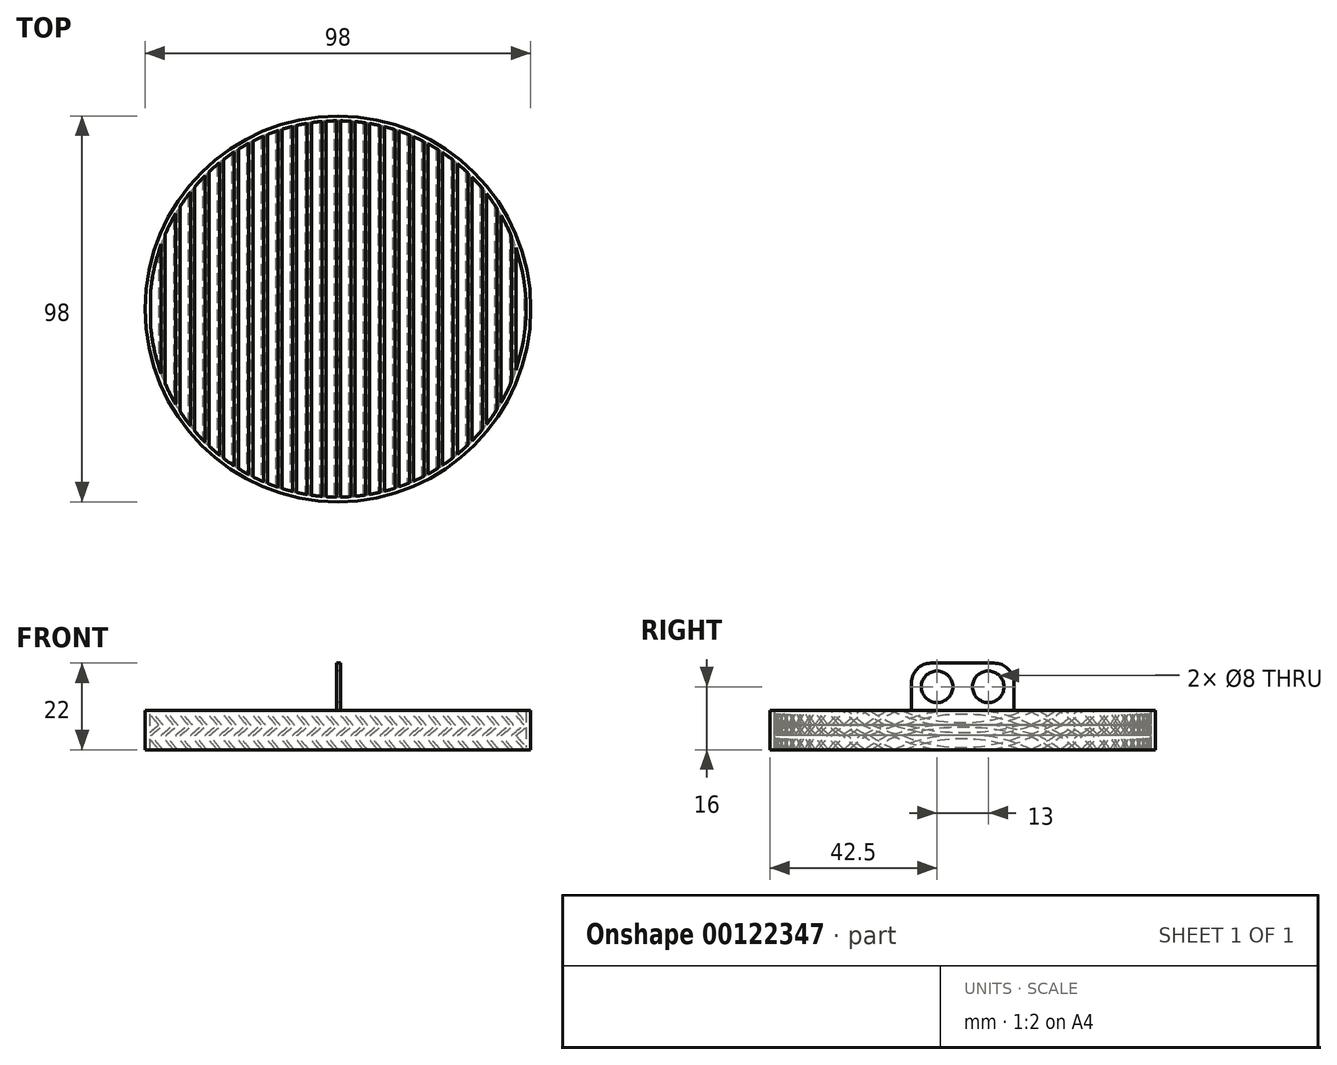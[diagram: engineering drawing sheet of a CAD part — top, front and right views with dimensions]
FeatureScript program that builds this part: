
annotation { "Feature Type Name" : "Feature", "Feature Type Description" : "" }
export const myFeature = defineFeature(function(context is Context, id is Id, definition is map)
    precondition{}
    {
        {
            var Q0;
            Q0=qCreatedBy(makeId("Top.planeOp"),FACE);
            var sketch = newSketch(context, id + "F0", { "sketchPlane" : qUnion([Q0])});
            skCircle(sketch, "E0", {"center": v(0, 0) * mm, "radius": 49 * mm});
            skCircle(sketch, "E1", {"center": v(0, 0) * mm, "radius": 47.8 * mm});
            skSolve(sketch);
        }
        {
            var Q0;
            Q0=makeQuery(id+"F0.imprint","IMPRINT",FACE,{"disambiguationData":[TD([[makeQuery(id+"F0.imprint","IMPRINT",EDGE,{"derivedFrom":sQuery(id+"F0.wireOp",EDGE,"E0")}),1.0]])]});
            extrude(context, id + "F1", {"entities" : qUnion([Q0]), "depth" : 10 * mm});
        }
        {
            var Q0;
            Q0=qCreatedBy(makeId("Front.planeOp"),FACE);
            var sketch = newSketch(context, id + "F2", { "sketchPlane" : qUnion([Q0])});
            skLineSegment(sketch, "E2", {"start": v(-45.5, 0) * mm, "end": v(-48.6, 3.7) * mm});
            skLineSegment(sketch, "E3", {"start": v(-48.6, 3.7) * mm, "end": v(-45.5, 6.3) * mm});
            skLineSegment(sketch, "E4", {"start": v(-45.5, 6.3) * mm, "end": v(-48.6, 10) * mm});
            skLineSegment(sketch, "E5.0", {"start": v(-44.37, 6.2) * mm, "end": v(-47.56, 10) * mm});
            skLineSegment(sketch, "E5.1", {"start": v(-47.47, 3.6) * mm, "end": v(-44.37, 6.2) * mm});
            skLineSegment(sketch, "E5.2", {"start": v(-44.45, 0) * mm, "end": v(-47.47, 3.6) * mm});
            skLineSegment(sketch, "E6", {"start": v(-48.6, 10) * mm, "end": v(-47.56, 10) * mm});
            skLineSegment(sketch, "E7", {"start": v(-45.5, 0) * mm, "end": v(-44.45, 0) * mm});
            skLineSegment(sketch, "E8.1.0.0", {"start": v(-40.74, 0) * mm, "end": v(-43.76, 3.6) * mm});
            skLineSegment(sketch, "E8.1.0.1", {"start": v(-43.76, 3.6) * mm, "end": v(-40.66, 6.2) * mm});
            skLineSegment(sketch, "E8.1.0.2", {"start": v(-44.9, 3.7) * mm, "end": v(-41.79, 6.3) * mm});
            skLineSegment(sketch, "E8.1.0.3", {"start": v(-40.66, 6.2) * mm, "end": v(-43.85, 10) * mm});
            skLineSegment(sketch, "E8.1.0.4", {"start": v(-41.79, 6.3) * mm, "end": v(-44.9, 10) * mm});
            skLineSegment(sketch, "E8.1.0.5", {"start": v(-41.79, 0) * mm, "end": v(-44.9, 3.7) * mm});
            skLineSegment(sketch, "E8.1.0.6", {"start": v(-44.9, 10) * mm, "end": v(-43.85, 10) * mm});
            skLineSegment(sketch, "E8.1.0.7", {"start": v(-41.79, 0) * mm, "end": v(-40.74, 0) * mm});
            skLineSegment(sketch, "E8.2.0.0", {"start": v(-37.03, 0) * mm, "end": v(-40.05, 3.6) * mm});
            skLineSegment(sketch, "E8.2.0.1", {"start": v(-40.05, 3.6) * mm, "end": v(-36.95, 6.2) * mm});
            skLineSegment(sketch, "E8.2.0.2", {"start": v(-41.18, 3.7) * mm, "end": v(-38.08, 6.3) * mm});
            skLineSegment(sketch, "E8.2.0.3", {"start": v(-36.95, 6.2) * mm, "end": v(-40.14, 10) * mm});
            skLineSegment(sketch, "E8.2.0.4", {"start": v(-38.08, 6.3) * mm, "end": v(-41.18, 10) * mm});
            skLineSegment(sketch, "E8.2.0.5", {"start": v(-38.08, 0) * mm, "end": v(-41.18, 3.7) * mm});
            skLineSegment(sketch, "E8.2.0.6", {"start": v(-41.18, 10) * mm, "end": v(-40.14, 10) * mm});
            skLineSegment(sketch, "E8.2.0.7", {"start": v(-38.08, 0) * mm, "end": v(-37.03, 0) * mm});
            skLineSegment(sketch, "E8.3.0.0", {"start": v(-33.32, 0) * mm, "end": v(-36.34, 3.6) * mm});
            skLineSegment(sketch, "E8.3.0.1", {"start": v(-36.34, 3.6) * mm, "end": v(-33.24, 6.2) * mm});
            skLineSegment(sketch, "E8.3.0.2", {"start": v(-37.47, 3.7) * mm, "end": v(-34.37, 6.3) * mm});
            skLineSegment(sketch, "E8.3.0.3", {"start": v(-33.24, 6.2) * mm, "end": v(-36.43, 10) * mm});
            skLineSegment(sketch, "E8.3.0.4", {"start": v(-34.37, 6.3) * mm, "end": v(-37.47, 10) * mm});
            skLineSegment(sketch, "E8.3.0.5", {"start": v(-34.37, 0) * mm, "end": v(-37.47, 3.7) * mm});
            skLineSegment(sketch, "E8.3.0.6", {"start": v(-37.47, 10) * mm, "end": v(-36.43, 10) * mm});
            skLineSegment(sketch, "E8.3.0.7", {"start": v(-34.37, 0) * mm, "end": v(-33.32, 0) * mm});
            skLineSegment(sketch, "E8.4.0.0", {"start": v(-29.61, 0) * mm, "end": v(-32.63, 3.6) * mm});
            skLineSegment(sketch, "E8.4.0.1", {"start": v(-32.63, 3.6) * mm, "end": v(-29.53, 6.2) * mm});
            skLineSegment(sketch, "E8.4.0.2", {"start": v(-33.76, 3.7) * mm, "end": v(-30.66, 6.3) * mm});
            skLineSegment(sketch, "E8.4.0.3", {"start": v(-29.53, 6.2) * mm, "end": v(-32.72, 10) * mm});
            skLineSegment(sketch, "E8.4.0.4", {"start": v(-30.66, 6.3) * mm, "end": v(-33.76, 10) * mm});
            skLineSegment(sketch, "E8.4.0.5", {"start": v(-30.66, 0) * mm, "end": v(-33.76, 3.7) * mm});
            skLineSegment(sketch, "E8.4.0.6", {"start": v(-33.76, 10) * mm, "end": v(-32.72, 10) * mm});
            skLineSegment(sketch, "E8.4.0.7", {"start": v(-30.66, 0) * mm, "end": v(-29.61, 0) * mm});
            skLineSegment(sketch, "E8.5.0.0", {"start": v(-25.9, 0) * mm, "end": v(-28.92, 3.6) * mm});
            skLineSegment(sketch, "E8.5.0.1", {"start": v(-28.92, 3.6) * mm, "end": v(-25.82, 6.2) * mm});
            skLineSegment(sketch, "E8.5.0.2", {"start": v(-30.05, 3.7) * mm, "end": v(-26.95, 6.3) * mm});
            skLineSegment(sketch, "E8.5.0.3", {"start": v(-25.82, 6.2) * mm, "end": v(-29, 10) * mm});
            skLineSegment(sketch, "E8.5.0.4", {"start": v(-26.95, 6.3) * mm, "end": v(-30.05, 10) * mm});
            skLineSegment(sketch, "E8.5.0.5", {"start": v(-26.95, 0) * mm, "end": v(-30.05, 3.7) * mm});
            skLineSegment(sketch, "E8.5.0.6", {"start": v(-30.05, 10) * mm, "end": v(-29, 10) * mm});
            skLineSegment(sketch, "E8.5.0.7", {"start": v(-26.95, 0) * mm, "end": v(-25.9, 0) * mm});
            skLineSegment(sketch, "E8.6.0.0", {"start": v(-22.2, 0) * mm, "end": v(-25.21, 3.6) * mm});
            skLineSegment(sketch, "E8.6.0.1", {"start": v(-25.21, 3.6) * mm, "end": v(-22.1, 6.2) * mm});
            skLineSegment(sketch, "E8.6.0.2", {"start": v(-26.34, 3.7) * mm, "end": v(-23.24, 6.3) * mm});
            skLineSegment(sketch, "E8.6.0.3", {"start": v(-22.1, 6.2) * mm, "end": v(-25.3, 10) * mm});
            skLineSegment(sketch, "E8.6.0.4", {"start": v(-23.24, 6.3) * mm, "end": v(-26.34, 10) * mm});
            skLineSegment(sketch, "E8.6.0.5", {"start": v(-23.24, 0) * mm, "end": v(-26.34, 3.7) * mm});
            skLineSegment(sketch, "E8.6.0.6", {"start": v(-26.34, 10) * mm, "end": v(-25.3, 10) * mm});
            skLineSegment(sketch, "E8.6.0.7", {"start": v(-23.24, 0) * mm, "end": v(-22.2, 0) * mm});
            skLineSegment(sketch, "E8.7.0.0", {"start": v(-18.48, 0) * mm, "end": v(-21.5, 3.6) * mm});
            skLineSegment(sketch, "E8.7.0.1", {"start": v(-21.5, 3.6) * mm, "end": v(-18.4, 6.2) * mm});
            skLineSegment(sketch, "E8.7.0.2", {"start": v(-22.63, 3.7) * mm, "end": v(-19.53, 6.3) * mm});
            skLineSegment(sketch, "E8.7.0.3", {"start": v(-18.4, 6.2) * mm, "end": v(-21.59, 10) * mm});
            skLineSegment(sketch, "E8.7.0.4", {"start": v(-19.53, 6.3) * mm, "end": v(-22.63, 10) * mm});
            skLineSegment(sketch, "E8.7.0.5", {"start": v(-19.53, 0) * mm, "end": v(-22.63, 3.7) * mm});
            skLineSegment(sketch, "E8.7.0.6", {"start": v(-22.63, 10) * mm, "end": v(-21.59, 10) * mm});
            skLineSegment(sketch, "E8.7.0.7", {"start": v(-19.53, 0) * mm, "end": v(-18.48, 0) * mm});
            skLineSegment(sketch, "E8.8.0.0", {"start": v(-14.77, 0) * mm, "end": v(-17.8, 3.6) * mm});
            skLineSegment(sketch, "E8.8.0.1", {"start": v(-17.8, 3.6) * mm, "end": v(-14.69, 6.2) * mm});
            skLineSegment(sketch, "E8.8.0.2", {"start": v(-18.92, 3.7) * mm, "end": v(-15.82, 6.3) * mm});
            skLineSegment(sketch, "E8.8.0.3", {"start": v(-14.69, 6.2) * mm, "end": v(-17.88, 10) * mm});
            skLineSegment(sketch, "E8.8.0.4", {"start": v(-15.82, 6.3) * mm, "end": v(-18.92, 10) * mm});
            skLineSegment(sketch, "E8.8.0.5", {"start": v(-15.82, 0) * mm, "end": v(-18.92, 3.7) * mm});
            skLineSegment(sketch, "E8.8.0.6", {"start": v(-18.92, 10) * mm, "end": v(-17.88, 10) * mm});
            skLineSegment(sketch, "E8.8.0.7", {"start": v(-15.82, 0) * mm, "end": v(-14.77, 0) * mm});
            skLineSegment(sketch, "E8.9.0.0", {"start": v(-11.06, 0) * mm, "end": v(-14.08, 3.6) * mm});
            skLineSegment(sketch, "E8.9.0.1", {"start": v(-14.08, 3.6) * mm, "end": v(-10.98, 6.2) * mm});
            skLineSegment(sketch, "E8.9.0.2", {"start": v(-15.2, 3.7) * mm, "end": v(-12.1, 6.3) * mm});
            skLineSegment(sketch, "E8.9.0.3", {"start": v(-10.98, 6.2) * mm, "end": v(-14.17, 10) * mm});
            skLineSegment(sketch, "E8.9.0.4", {"start": v(-12.1, 6.3) * mm, "end": v(-15.2, 10) * mm});
            skLineSegment(sketch, "E8.9.0.5", {"start": v(-12.1, 0) * mm, "end": v(-15.21, 3.7) * mm});
            skLineSegment(sketch, "E8.9.0.6", {"start": v(-15.2, 10) * mm, "end": v(-14.17, 10) * mm});
            skLineSegment(sketch, "E8.9.0.7", {"start": v(-12.1, 0) * mm, "end": v(-11.06, 0) * mm});
            skLineSegment(sketch, "E8.10.0.0", {"start": v(-7.35, 0) * mm, "end": v(-10.37, 3.6) * mm});
            skLineSegment(sketch, "E8.10.0.1", {"start": v(-10.37, 3.6) * mm, "end": v(-7.27, 6.2) * mm});
            skLineSegment(sketch, "E8.10.0.2", {"start": v(-11.5, 3.7) * mm, "end": v(-8.4, 6.3) * mm});
            skLineSegment(sketch, "E8.10.0.3", {"start": v(-7.27, 6.2) * mm, "end": v(-10.46, 10) * mm});
            skLineSegment(sketch, "E8.10.0.4", {"start": v(-8.4, 6.3) * mm, "end": v(-11.5, 10) * mm});
            skLineSegment(sketch, "E8.10.0.5", {"start": v(-8.4, 0) * mm, "end": v(-11.5, 3.7) * mm});
            skLineSegment(sketch, "E8.10.0.6", {"start": v(-11.5, 10) * mm, "end": v(-10.46, 10) * mm});
            skLineSegment(sketch, "E8.10.0.7", {"start": v(-8.4, 0) * mm, "end": v(-7.35, 0) * mm});
            skLineSegment(sketch, "E8.11.0.0", {"start": v(-3.64, 0) * mm, "end": v(-6.66, 3.6) * mm});
            skLineSegment(sketch, "E8.11.0.1", {"start": v(-6.66, 3.6) * mm, "end": v(-3.56, 6.2) * mm});
            skLineSegment(sketch, "E8.11.0.2", {"start": v(-7.79, 3.7) * mm, "end": v(-4.69, 6.3) * mm});
            skLineSegment(sketch, "E8.11.0.3", {"start": v(-3.56, 6.2) * mm, "end": v(-6.75, 10) * mm});
            skLineSegment(sketch, "E8.11.0.4", {"start": v(-4.69, 6.3) * mm, "end": v(-7.8, 10) * mm});
            skLineSegment(sketch, "E8.11.0.5", {"start": v(-4.69, 0) * mm, "end": v(-7.8, 3.7) * mm});
            skLineSegment(sketch, "E8.11.0.6", {"start": v(-7.79, 10) * mm, "end": v(-6.75, 10) * mm});
            skLineSegment(sketch, "E8.11.0.7", {"start": v(-4.69, 0) * mm, "end": v(-3.64, 0) * mm});
            skLineSegment(sketch, "E8.12.0.0", {"start": v(0.07, 0) * mm, "end": v(-2.95, 3.6) * mm});
            skLineSegment(sketch, "E8.12.0.1", {"start": v(-2.95, 3.6) * mm, "end": v(0.15, 6.2) * mm});
            skLineSegment(sketch, "E8.12.0.2", {"start": v(-4.08, 3.7) * mm, "end": v(-0.98, 6.3) * mm});
            skLineSegment(sketch, "E8.12.0.3", {"start": v(0.15, 6.2) * mm, "end": v(-3.04, 10) * mm});
            skLineSegment(sketch, "E8.12.0.4", {"start": v(-0.98, 6.3) * mm, "end": v(-4.08, 10) * mm});
            skLineSegment(sketch, "E8.12.0.5", {"start": v(-0.98, 0) * mm, "end": v(-4.08, 3.7) * mm});
            skLineSegment(sketch, "E8.12.0.6", {"start": v(-4.08, 10) * mm, "end": v(-3.04, 10) * mm});
            skLineSegment(sketch, "E8.12.0.7", {"start": v(-0.98, 0) * mm, "end": v(0.07, 0) * mm});
            skLineSegment(sketch, "E8.13.0.0", {"start": v(3.78, 0) * mm, "end": v(0.76, 3.6) * mm});
            skLineSegment(sketch, "E8.13.0.1", {"start": v(0.76, 3.6) * mm, "end": v(3.86, 6.2) * mm});
            skLineSegment(sketch, "E8.13.0.2", {"start": v(-0.37, 3.7) * mm, "end": v(2.73, 6.3) * mm});
            skLineSegment(sketch, "E8.13.0.3", {"start": v(3.86, 6.2) * mm, "end": v(0.67, 10) * mm});
            skLineSegment(sketch, "E8.13.0.4", {"start": v(2.73, 6.3) * mm, "end": v(-0.37, 10) * mm});
            skLineSegment(sketch, "E8.13.0.5", {"start": v(2.73, 0) * mm, "end": v(-0.37, 3.7) * mm});
            skLineSegment(sketch, "E8.13.0.6", {"start": v(-0.37, 10) * mm, "end": v(0.67, 10) * mm});
            skLineSegment(sketch, "E8.13.0.7", {"start": v(2.73, 0) * mm, "end": v(3.78, 0) * mm});
            skLineSegment(sketch, "E8.14.0.0", {"start": v(7.49, 0) * mm, "end": v(4.47, 3.6) * mm});
            skLineSegment(sketch, "E8.14.0.1", {"start": v(4.47, 3.6) * mm, "end": v(7.57, 6.2) * mm});
            skLineSegment(sketch, "E8.14.0.2", {"start": v(3.34, 3.7) * mm, "end": v(6.44, 6.3) * mm});
            skLineSegment(sketch, "E8.14.0.3", {"start": v(7.57, 6.2) * mm, "end": v(4.38, 10) * mm});
            skLineSegment(sketch, "E8.14.0.4", {"start": v(6.44, 6.3) * mm, "end": v(3.34, 10) * mm});
            skLineSegment(sketch, "E8.14.0.5", {"start": v(6.44, 0) * mm, "end": v(3.34, 3.7) * mm});
            skLineSegment(sketch, "E8.14.0.6", {"start": v(3.34, 10) * mm, "end": v(4.38, 10) * mm});
            skLineSegment(sketch, "E8.14.0.7", {"start": v(6.44, 0) * mm, "end": v(7.49, 0) * mm});
            skLineSegment(sketch, "E8.direction1", {"start": v(-45.5, 0) * mm, "end": v(-41.79, 0) * mm, "construction": true});
            skLineSegment(sketch, "E9.0.15.0", {"start": v(11.2, 0) * mm, "end": v(8.18, 3.6) * mm});
            skLineSegment(sketch, "E9.3.15.0", {"start": v(8.18, 3.6) * mm, "end": v(11.28, 6.2) * mm});
            skLineSegment(sketch, "E9.6.15.0", {"start": v(7.05, 3.7) * mm, "end": v(10.15, 6.3) * mm});
            skLineSegment(sketch, "E9.9.15.0", {"start": v(11.28, 6.2) * mm, "end": v(8.1, 10) * mm});
            skLineSegment(sketch, "E9.12.15.0", {"start": v(10.15, 6.3) * mm, "end": v(7.05, 10) * mm});
            skLineSegment(sketch, "E9.15.15.0", {"start": v(10.15, 0) * mm, "end": v(7.05, 3.7) * mm});
            skLineSegment(sketch, "E9.18.15.0", {"start": v(7.05, 10) * mm, "end": v(8.1, 10) * mm});
            skLineSegment(sketch, "E9.21.15.0", {"start": v(10.15, 0) * mm, "end": v(11.2, 0) * mm});
            skLineSegment(sketch, "E9.0.16.0", {"start": v(14.9, 0) * mm, "end": v(11.89, 3.6) * mm});
            skLineSegment(sketch, "E9.3.16.0", {"start": v(11.89, 3.6) * mm, "end": v(15, 6.2) * mm});
            skLineSegment(sketch, "E9.6.16.0", {"start": v(10.76, 3.7) * mm, "end": v(13.86, 6.3) * mm});
            skLineSegment(sketch, "E9.9.16.0", {"start": v(15, 6.2) * mm, "end": v(11.8, 10) * mm});
            skLineSegment(sketch, "E9.12.16.0", {"start": v(13.86, 6.3) * mm, "end": v(10.76, 10) * mm});
            skLineSegment(sketch, "E9.15.16.0", {"start": v(13.86, 0) * mm, "end": v(10.76, 3.7) * mm});
            skLineSegment(sketch, "E9.18.16.0", {"start": v(10.76, 10) * mm, "end": v(11.8, 10) * mm});
            skLineSegment(sketch, "E9.21.16.0", {"start": v(13.86, 0) * mm, "end": v(14.9, 0) * mm});
            skLineSegment(sketch, "E9.0.17.0", {"start": v(18.62, 0) * mm, "end": v(15.6, 3.6) * mm});
            skLineSegment(sketch, "E9.3.17.0", {"start": v(15.6, 3.6) * mm, "end": v(18.7, 6.2) * mm});
            skLineSegment(sketch, "E9.6.17.0", {"start": v(14.47, 3.7) * mm, "end": v(17.57, 6.3) * mm});
            skLineSegment(sketch, "E9.9.17.0", {"start": v(18.7, 6.2) * mm, "end": v(15.51, 10) * mm});
            skLineSegment(sketch, "E9.12.17.0", {"start": v(17.57, 6.3) * mm, "end": v(14.47, 10) * mm});
            skLineSegment(sketch, "E9.15.17.0", {"start": v(17.57, 0) * mm, "end": v(14.47, 3.7) * mm});
            skLineSegment(sketch, "E9.18.17.0", {"start": v(14.47, 10) * mm, "end": v(15.51, 10) * mm});
            skLineSegment(sketch, "E9.21.17.0", {"start": v(17.57, 0) * mm, "end": v(18.62, 0) * mm});
            skLineSegment(sketch, "E9.0.18.0", {"start": v(22.33, 0) * mm, "end": v(19.3, 3.6) * mm});
            skLineSegment(sketch, "E9.3.18.0", {"start": v(19.3, 3.6) * mm, "end": v(22.41, 6.2) * mm});
            skLineSegment(sketch, "E9.6.18.0", {"start": v(18.18, 3.7) * mm, "end": v(21.28, 6.3) * mm});
            skLineSegment(sketch, "E9.9.18.0", {"start": v(22.41, 6.2) * mm, "end": v(19.22, 10) * mm});
            skLineSegment(sketch, "E9.12.18.0", {"start": v(21.28, 6.3) * mm, "end": v(18.18, 10) * mm});
            skLineSegment(sketch, "E9.15.18.0", {"start": v(21.28, 0) * mm, "end": v(18.18, 3.7) * mm});
            skLineSegment(sketch, "E9.18.18.0", {"start": v(18.18, 10) * mm, "end": v(19.22, 10) * mm});
            skLineSegment(sketch, "E9.21.18.0", {"start": v(21.28, 0) * mm, "end": v(22.33, 0) * mm});
            skLineSegment(sketch, "E9.0.19.0", {"start": v(26.04, 0) * mm, "end": v(23.02, 3.6) * mm});
            skLineSegment(sketch, "E9.3.19.0", {"start": v(23.02, 3.6) * mm, "end": v(26.12, 6.2) * mm});
            skLineSegment(sketch, "E9.6.19.0", {"start": v(21.89, 3.7) * mm, "end": v(25, 6.3) * mm});
            skLineSegment(sketch, "E9.9.19.0", {"start": v(26.12, 6.2) * mm, "end": v(22.93, 10) * mm});
            skLineSegment(sketch, "E9.12.19.0", {"start": v(25, 6.3) * mm, "end": v(21.9, 10) * mm});
            skLineSegment(sketch, "E9.15.19.0", {"start": v(25, 0) * mm, "end": v(21.89, 3.7) * mm});
            skLineSegment(sketch, "E9.18.19.0", {"start": v(21.9, 10) * mm, "end": v(22.93, 10) * mm});
            skLineSegment(sketch, "E9.21.19.0", {"start": v(25, 0) * mm, "end": v(26.04, 0) * mm});
            skLineSegment(sketch, "E10.0.20.0", {"start": v(29.75, 0) * mm, "end": v(26.73, 3.6) * mm});
            skLineSegment(sketch, "E10.3.20.0", {"start": v(26.73, 3.6) * mm, "end": v(29.83, 6.2) * mm});
            skLineSegment(sketch, "E10.6.20.0", {"start": v(25.6, 3.7) * mm, "end": v(28.7, 6.3) * mm});
            skLineSegment(sketch, "E10.9.20.0", {"start": v(29.83, 6.2) * mm, "end": v(26.64, 10) * mm});
            skLineSegment(sketch, "E10.12.20.0", {"start": v(28.7, 6.3) * mm, "end": v(25.6, 10) * mm});
            skLineSegment(sketch, "E10.15.20.0", {"start": v(28.7, 0) * mm, "end": v(25.6, 3.7) * mm});
            skLineSegment(sketch, "E10.18.20.0", {"start": v(25.6, 10) * mm, "end": v(26.64, 10) * mm});
            skLineSegment(sketch, "E10.21.20.0", {"start": v(28.7, 0) * mm, "end": v(29.75, 0) * mm});
            skLineSegment(sketch, "E10.0.21.0", {"start": v(33.46, 0) * mm, "end": v(30.44, 3.6) * mm});
            skLineSegment(sketch, "E10.3.21.0", {"start": v(30.44, 3.6) * mm, "end": v(33.54, 6.2) * mm});
            skLineSegment(sketch, "E10.6.21.0", {"start": v(29.3, 3.7) * mm, "end": v(32.41, 6.3) * mm});
            skLineSegment(sketch, "E10.9.21.0", {"start": v(33.54, 6.2) * mm, "end": v(30.35, 10) * mm});
            skLineSegment(sketch, "E10.12.21.0", {"start": v(32.41, 6.3) * mm, "end": v(29.31, 10) * mm});
            skLineSegment(sketch, "E10.15.21.0", {"start": v(32.41, 0) * mm, "end": v(29.3, 3.7) * mm});
            skLineSegment(sketch, "E10.18.21.0", {"start": v(29.31, 10) * mm, "end": v(30.35, 10) * mm});
            skLineSegment(sketch, "E10.21.21.0", {"start": v(32.41, 0) * mm, "end": v(33.46, 0) * mm});
            skLineSegment(sketch, "E10.0.22.0", {"start": v(37.17, 0) * mm, "end": v(34.15, 3.6) * mm});
            skLineSegment(sketch, "E10.3.22.0", {"start": v(34.15, 3.6) * mm, "end": v(37.25, 6.2) * mm});
            skLineSegment(sketch, "E10.6.22.0", {"start": v(33.02, 3.7) * mm, "end": v(36.12, 6.3) * mm});
            skLineSegment(sketch, "E10.9.22.0", {"start": v(37.25, 6.2) * mm, "end": v(34.06, 10) * mm});
            skLineSegment(sketch, "E10.12.22.0", {"start": v(36.12, 6.3) * mm, "end": v(33.02, 10) * mm});
            skLineSegment(sketch, "E10.15.22.0", {"start": v(36.12, 0) * mm, "end": v(33.02, 3.7) * mm});
            skLineSegment(sketch, "E10.18.22.0", {"start": v(33.02, 10) * mm, "end": v(34.06, 10) * mm});
            skLineSegment(sketch, "E10.21.22.0", {"start": v(36.12, 0) * mm, "end": v(37.17, 0) * mm});
            skLineSegment(sketch, "E10.0.23.0", {"start": v(40.88, 0) * mm, "end": v(37.86, 3.6) * mm});
            skLineSegment(sketch, "E10.3.23.0", {"start": v(37.86, 3.6) * mm, "end": v(40.96, 6.2) * mm});
            skLineSegment(sketch, "E10.6.23.0", {"start": v(36.73, 3.7) * mm, "end": v(39.83, 6.3) * mm});
            skLineSegment(sketch, "E10.9.23.0", {"start": v(40.96, 6.2) * mm, "end": v(37.77, 10) * mm});
            skLineSegment(sketch, "E10.12.23.0", {"start": v(39.83, 6.3) * mm, "end": v(36.73, 10) * mm});
            skLineSegment(sketch, "E10.15.23.0", {"start": v(39.83, 0) * mm, "end": v(36.73, 3.7) * mm});
            skLineSegment(sketch, "E10.18.23.0", {"start": v(36.73, 10) * mm, "end": v(37.77, 10) * mm});
            skLineSegment(sketch, "E10.21.23.0", {"start": v(39.83, 0) * mm, "end": v(40.88, 0) * mm});
            skLineSegment(sketch, "E11.0.24.0", {"start": v(44.59, 0) * mm, "end": v(41.57, 3.6) * mm});
            skLineSegment(sketch, "E11.3.24.0", {"start": v(41.57, 3.6) * mm, "end": v(44.67, 6.2) * mm});
            skLineSegment(sketch, "E11.6.24.0", {"start": v(40.44, 3.7) * mm, "end": v(43.54, 6.3) * mm});
            skLineSegment(sketch, "E11.9.24.0", {"start": v(44.67, 6.2) * mm, "end": v(41.48, 10) * mm});
            skLineSegment(sketch, "E11.12.24.0", {"start": v(43.54, 6.3) * mm, "end": v(40.44, 10) * mm});
            skLineSegment(sketch, "E11.15.24.0", {"start": v(43.54, 0) * mm, "end": v(40.44, 3.7) * mm});
            skLineSegment(sketch, "E11.18.24.0", {"start": v(40.44, 10) * mm, "end": v(41.48, 10) * mm});
            skLineSegment(sketch, "E11.21.24.0", {"start": v(43.54, 0) * mm, "end": v(44.59, 0) * mm});
            skLineSegment(sketch, "E12.0.25.0", {"start": v(48.3, 0) * mm, "end": v(45.28, 3.6) * mm});
            skLineSegment(sketch, "E12.3.25.0", {"start": v(45.28, 3.6) * mm, "end": v(48.38, 6.2) * mm});
            skLineSegment(sketch, "E12.6.25.0", {"start": v(44.15, 3.7) * mm, "end": v(47.25, 6.3) * mm});
            skLineSegment(sketch, "E12.9.25.0", {"start": v(48.38, 6.2) * mm, "end": v(45.2, 10) * mm});
            skLineSegment(sketch, "E12.12.25.0", {"start": v(47.25, 6.3) * mm, "end": v(44.15, 10) * mm});
            skLineSegment(sketch, "E12.15.25.0", {"start": v(47.25, 0) * mm, "end": v(44.15, 3.7) * mm});
            skLineSegment(sketch, "E12.18.25.0", {"start": v(44.15, 10) * mm, "end": v(45.2, 10) * mm});
            skLineSegment(sketch, "E12.21.25.0", {"start": v(47.25, 0) * mm, "end": v(48.3, 0) * mm});
            skSolve(sketch);
        }
        {
            var Q0;
            Q0=makeQuery(id+"F2.imprint","IMPRINT",FACE,{"disambiguationData":[TD([[makeQuery(id+"F2.imprint","IMPRINT",EDGE,{"derivedFrom":sQuery(id+"F2.wireOp",EDGE,"E2")}),-1.0]])]});
            var Q1;
            Q1=makeQuery(id+"F2.imprint","IMPRINT",FACE,{"disambiguationData":[TD([[makeQuery(id+"F2.imprint","IMPRINT",EDGE,{"derivedFrom":sQuery(id+"F2.wireOp",EDGE,"E8.1.0.0")}),1.0]])]});
            var Q2;
            Q2=makeQuery(id+"F2.imprint","IMPRINT",FACE,{"disambiguationData":[TD([[makeQuery(id+"F2.imprint","IMPRINT",EDGE,{"derivedFrom":sQuery(id+"F2.wireOp",EDGE,"E8.2.0.0")}),1.0]])]});
            var Q3;
            Q3=makeQuery(id+"F2.imprint","IMPRINT",FACE,{"disambiguationData":[TD([[makeQuery(id+"F2.imprint","IMPRINT",EDGE,{"derivedFrom":sQuery(id+"F2.wireOp",EDGE,"E8.3.0.0")}),1.0]])]});
            var Q4;
            Q4=makeQuery(id+"F2.imprint","IMPRINT",FACE,{"disambiguationData":[TD([[makeQuery(id+"F2.imprint","IMPRINT",EDGE,{"derivedFrom":sQuery(id+"F2.wireOp",EDGE,"E8.4.0.0")}),1.0]])]});
            var Q5;
            Q5=makeQuery(id+"F2.imprint","IMPRINT",FACE,{"disambiguationData":[TD([[makeQuery(id+"F2.imprint","IMPRINT",EDGE,{"derivedFrom":sQuery(id+"F2.wireOp",EDGE,"E8.5.0.0")}),1.0]])]});
            var Q6;
            Q6=makeQuery(id+"F2.imprint","IMPRINT",FACE,{"disambiguationData":[TD([[makeQuery(id+"F2.imprint","IMPRINT",EDGE,{"derivedFrom":sQuery(id+"F2.wireOp",EDGE,"E8.6.0.0")}),1.0]])]});
            var Q7;
            Q7=makeQuery(id+"F2.imprint","IMPRINT",FACE,{"disambiguationData":[TD([[makeQuery(id+"F2.imprint","IMPRINT",EDGE,{"derivedFrom":sQuery(id+"F2.wireOp",EDGE,"E8.7.0.0")}),1.0]])]});
            var Q8;
            Q8=makeQuery(id+"F2.imprint","IMPRINT",FACE,{"disambiguationData":[TD([[makeQuery(id+"F2.imprint","IMPRINT",EDGE,{"derivedFrom":sQuery(id+"F2.wireOp",EDGE,"E8.8.0.0")}),1.0]])]});
            var Q9;
            Q9=makeQuery(id+"F2.imprint","IMPRINT",FACE,{"disambiguationData":[TD([[makeQuery(id+"F2.imprint","IMPRINT",EDGE,{"derivedFrom":sQuery(id+"F2.wireOp",EDGE,"E8.9.0.0")}),1.0]])]});
            var Q10;
            Q10=makeQuery(id+"F2.imprint","IMPRINT",FACE,{"disambiguationData":[TD([[makeQuery(id+"F2.imprint","IMPRINT",EDGE,{"derivedFrom":sQuery(id+"F2.wireOp",EDGE,"E8.10.0.0")}),1.0]])]});
            var Q11;
            Q11=makeQuery(id+"F2.imprint","IMPRINT",FACE,{"disambiguationData":[TD([[makeQuery(id+"F2.imprint","IMPRINT",EDGE,{"derivedFrom":sQuery(id+"F2.wireOp",EDGE,"E8.11.0.0")}),1.0]])]});
            var Q12;
            Q12=makeQuery(id+"F2.imprint","IMPRINT",FACE,{"disambiguationData":[TD([[makeQuery(id+"F2.imprint","IMPRINT",EDGE,{"derivedFrom":sQuery(id+"F2.wireOp",EDGE,"E8.12.0.0")}),1.0]])]});
            var Q13;
            Q13=makeQuery(id+"F2.imprint","IMPRINT",FACE,{"disambiguationData":[TD([[makeQuery(id+"F2.imprint","IMPRINT",EDGE,{"derivedFrom":sQuery(id+"F2.wireOp",EDGE,"E8.13.0.0")}),1.0]])]});
            var Q14;
            Q14=makeQuery(id+"F2.imprint","IMPRINT",FACE,{"disambiguationData":[TD([[makeQuery(id+"F2.imprint","IMPRINT",EDGE,{"derivedFrom":sQuery(id+"F2.wireOp",EDGE,"E8.14.0.0")}),1.0]])]});
            var Q15;
            Q15=makeQuery(id+"F2.imprint","IMPRINT",FACE,{"disambiguationData":[TD([[makeQuery(id+"F2.imprint","IMPRINT",EDGE,{"derivedFrom":sQuery(id+"F2.wireOp",EDGE,"E9.0.15.0")}),1.0]])]});
            var Q16;
            Q16=makeQuery(id+"F2.imprint","IMPRINT",FACE,{"disambiguationData":[TD([[makeQuery(id+"F2.imprint","IMPRINT",EDGE,{"derivedFrom":sQuery(id+"F2.wireOp",EDGE,"E9.0.16.0")}),1.0]])]});
            var Q17;
            Q17=makeQuery(id+"F2.imprint","IMPRINT",FACE,{"disambiguationData":[TD([[makeQuery(id+"F2.imprint","IMPRINT",EDGE,{"derivedFrom":sQuery(id+"F2.wireOp",EDGE,"E9.0.17.0")}),1.0]])]});
            var Q18;
            Q18=makeQuery(id+"F2.imprint","IMPRINT",FACE,{"disambiguationData":[TD([[makeQuery(id+"F2.imprint","IMPRINT",EDGE,{"derivedFrom":sQuery(id+"F2.wireOp",EDGE,"E9.0.18.0")}),1.0]])]});
            var Q19;
            Q19=makeQuery(id+"F2.imprint","IMPRINT",FACE,{"disambiguationData":[TD([[makeQuery(id+"F2.imprint","IMPRINT",EDGE,{"derivedFrom":sQuery(id+"F2.wireOp",EDGE,"E9.0.19.0")}),1.0]])]});
            var Q20;
            Q20=makeQuery(id+"F2.imprint","IMPRINT",FACE,{"disambiguationData":[TD([[makeQuery(id+"F2.imprint","IMPRINT",EDGE,{"derivedFrom":sQuery(id+"F2.wireOp",EDGE,"E10.0.20.0")}),1.0]])]});
            var Q21;
            Q21=makeQuery(id+"F2.imprint","IMPRINT",FACE,{"disambiguationData":[TD([[makeQuery(id+"F2.imprint","IMPRINT",EDGE,{"derivedFrom":sQuery(id+"F2.wireOp",EDGE,"E10.0.21.0")}),1.0]])]});
            var Q22;
            Q22=makeQuery(id+"F2.imprint","IMPRINT",FACE,{"disambiguationData":[TD([[makeQuery(id+"F2.imprint","IMPRINT",EDGE,{"derivedFrom":sQuery(id+"F2.wireOp",EDGE,"E10.0.22.0")}),1.0]])]});
            var Q23;
            Q23=makeQuery(id+"F2.imprint","IMPRINT",FACE,{"disambiguationData":[TD([[makeQuery(id+"F2.imprint","IMPRINT",EDGE,{"derivedFrom":sQuery(id+"F2.wireOp",EDGE,"E10.0.23.0")}),1.0]])]});
            var Q24;
            Q24=makeQuery(id+"F2.imprint","IMPRINT",FACE,{"disambiguationData":[TD([[makeQuery(id+"F2.imprint","IMPRINT",EDGE,{"derivedFrom":sQuery(id+"F2.wireOp",EDGE,"E11.0.24.0")}),1.0]])]});
            var Q25;
            Q25=makeQuery(id+"F2.imprint","IMPRINT",FACE,{"disambiguationData":[TD([[makeQuery(id+"F2.imprint","IMPRINT",EDGE,{"derivedFrom":sQuery(id+"F2.wireOp",EDGE,"E12.0.25.0")}),1.0]])]});
            var Q26;
            Q26=makeQuery(id+"F1.opExtrude","SWEPT_FACE",FACE,{"disambiguationData":[OSD([sQuery(id+"F0.wireOp",EDGE,"E1")])]});
            var Q27;
            Q27=makeQuery(id+"F1.opExtrude","SWEPT_BODY",BODY,{"disambiguationData":[OSD([sQuery(id+"F0.wireOp",EDGE,"E0"),sQuery(id+"F0.wireOp",EDGE,"E1")])]});
            extrude(context, id + "F3", {"entities" : qUnion([Q0, Q1, Q2, Q3, Q4, Q5, Q6, Q7, Q8, Q9, Q10, Q11, Q12, Q13, Q14, Q15, Q16, Q17, Q18, Q19, Q20, Q21, Q22, Q23, Q24, Q25]), "operationType" : NewBodyOperationType.ADD, "endBound" : BoundingType.UP_TO_BODY, "oppositeDirection" : true, "endBoundEntityFace" : qUnion([Q26]), "endBoundEntityBody" : qUnion([Q27]), "depth" : 25 * mm});
        }
        {
            var Q0;
            Q0=makeQuery(id+"F1.opExtrude","SWEPT_BODY",BODY,{"disambiguationData":[OSD([sQuery(id+"F0.wireOp",EDGE,"E0"),sQuery(id+"F0.wireOp",EDGE,"E1")])]});
            var Q1;
            Q1=qCreatedBy(makeId("Front.planeOp"),FACE);
            mirror(context, id + "F4", {"operationType" : NewBodyOperationType.ADD, "entities" : qUnion([Q0]), "mirrorPlane" : qUnion([Q1])});
        }
        {
            var Q0;
            {var subQ0=makeQuery(id+"F3.boolean.opBoolean","MERGE",FACE,{"derivedFrom":[makeQuery(id+"F1.opExtrude","CAP_FACE",FACE,{"disambiguationData":[OSD([sQuery(id+"F0.wireOp",EDGE,"E0"),sQuery(id+"F0.wireOp",EDGE,"E1")])],"isStart":false}),makeQuery(id+"F3.opExtrude","SWEPT_FACE",FACE,{"disambiguationData":[OSD([sQuery(id+"F2.wireOp",EDGE,"E6")])]}),makeQuery(id+"F3.opExtrude","SWEPT_FACE",FACE,{"disambiguationData":[OSD([sQuery(id+"F2.wireOp",EDGE,"E8.1.0.6")])]}),makeQuery(id+"F3.opExtrude","SWEPT_FACE",FACE,{"disambiguationData":[OSD([sQuery(id+"F2.wireOp",EDGE,"E8.2.0.6")])]}),makeQuery(id+"F3.opExtrude","SWEPT_FACE",FACE,{"disambiguationData":[OSD([sQuery(id+"F2.wireOp",EDGE,"E8.3.0.6")])]}),makeQuery(id+"F3.opExtrude","SWEPT_FACE",FACE,{"disambiguationData":[OSD([sQuery(id+"F2.wireOp",EDGE,"E8.4.0.6")])]}),makeQuery(id+"F3.opExtrude","SWEPT_FACE",FACE,{"disambiguationData":[OSD([sQuery(id+"F2.wireOp",EDGE,"E8.5.0.6")])]}),makeQuery(id+"F3.opExtrude","SWEPT_FACE",FACE,{"disambiguationData":[OSD([sQuery(id+"F2.wireOp",EDGE,"E8.6.0.6")])]}),makeQuery(id+"F3.opExtrude","SWEPT_FACE",FACE,{"disambiguationData":[OSD([sQuery(id+"F2.wireOp",EDGE,"E8.7.0.6")])]}),makeQuery(id+"F3.opExtrude","SWEPT_FACE",FACE,{"disambiguationData":[OSD([sQuery(id+"F2.wireOp",EDGE,"E8.8.0.6")])]}),makeQuery(id+"F3.opExtrude","SWEPT_FACE",FACE,{"disambiguationData":[OSD([sQuery(id+"F2.wireOp",EDGE,"E8.9.0.6")])]}),makeQuery(id+"F3.opExtrude","SWEPT_FACE",FACE,{"disambiguationData":[OSD([sQuery(id+"F2.wireOp",EDGE,"E8.10.0.6")])]}),makeQuery(id+"F3.opExtrude","SWEPT_FACE",FACE,{"disambiguationData":[OSD([sQuery(id+"F2.wireOp",EDGE,"E8.11.0.6")])]}),makeQuery(id+"F3.opExtrude","SWEPT_FACE",FACE,{"disambiguationData":[OSD([sQuery(id+"F2.wireOp",EDGE,"E8.12.0.6")])]}),makeQuery(id+"F3.opExtrude","SWEPT_FACE",FACE,{"disambiguationData":[OSD([sQuery(id+"F2.wireOp",EDGE,"E8.13.0.6")])]}),makeQuery(id+"F3.opExtrude","SWEPT_FACE",FACE,{"disambiguationData":[OSD([sQuery(id+"F2.wireOp",EDGE,"E8.14.0.6")])]}),makeQuery(id+"F3.opExtrude","SWEPT_FACE",FACE,{"disambiguationData":[OSD([sQuery(id+"F2.wireOp",EDGE,"E9.18.15.0")])]}),makeQuery(id+"F3.opExtrude","SWEPT_FACE",FACE,{"disambiguationData":[OSD([sQuery(id+"F2.wireOp",EDGE,"E9.18.16.0")])]}),makeQuery(id+"F3.opExtrude","SWEPT_FACE",FACE,{"disambiguationData":[OSD([sQuery(id+"F2.wireOp",EDGE,"E9.18.17.0")])]}),makeQuery(id+"F3.opExtrude","SWEPT_FACE",FACE,{"disambiguationData":[OSD([sQuery(id+"F2.wireOp",EDGE,"E9.18.18.0")])]}),makeQuery(id+"F3.opExtrude","SWEPT_FACE",FACE,{"disambiguationData":[OSD([sQuery(id+"F2.wireOp",EDGE,"E9.18.19.0")])]}),makeQuery(id+"F3.opExtrude","SWEPT_FACE",FACE,{"disambiguationData":[OSD([sQuery(id+"F2.wireOp",EDGE,"E10.18.20.0")])]}),makeQuery(id+"F3.opExtrude","SWEPT_FACE",FACE,{"disambiguationData":[OSD([sQuery(id+"F2.wireOp",EDGE,"E10.18.21.0")])]}),makeQuery(id+"F3.opExtrude","SWEPT_FACE",FACE,{"disambiguationData":[OSD([sQuery(id+"F2.wireOp",EDGE,"E10.18.22.0")])]}),makeQuery(id+"F3.opExtrude","SWEPT_FACE",FACE,{"disambiguationData":[OSD([sQuery(id+"F2.wireOp",EDGE,"E10.18.23.0")])]}),makeQuery(id+"F3.opExtrude","SWEPT_FACE",FACE,{"disambiguationData":[OSD([sQuery(id+"F2.wireOp",EDGE,"E11.18.24.0")])]}),makeQuery(id+"F3.opExtrude","SWEPT_FACE",FACE,{"disambiguationData":[OSD([sQuery(id+"F2.wireOp",EDGE,"E12.18.25.0")])]})]});Q0=makeQuery(id+"F4.boolean.opBoolean","MERGE",FACE,{"derivedFrom":[subQ0,makeQuery(id+"F4.opPattern","COPY",FACE,{"derivedFrom":subQ0,"instanceName":"1"})]});}
            var sketch = newSketch(context, id + "F5", { "sketchPlane" : qUnion([Q0])});
            skLineSegment(sketch, "E13.bottom", {"start": v(-0.37, 13) * mm, "end": v(0.67, 13) * mm});
            skLineSegment(sketch, "E13.top", {"start": v(-0.37, -13) * mm, "end": v(0.67, -13) * mm});
            skLineSegment(sketch, "E13.left", {"start": v(-0.37, 13) * mm, "end": v(-0.37, -13) * mm});
            skLineSegment(sketch, "E13.right", {"start": v(0.67, 13) * mm, "end": v(0.67, -13) * mm});
            skSolve(sketch);
        }
        {
            var Q0;
            Q0 = qSketchRegion(id + "F5", true);
            extrude(context, id + "F6", {"entities" : qUnion([Q0]), "operationType" : NewBodyOperationType.ADD, "depth" : 12 * mm});
        }
        {
            var Q0;
            Q0=makeQuery(id+"F6.opExtrude","SWEPT_FACE",FACE,{"disambiguationData":[OSD([sQuery(id+"F5.wireOp",EDGE,"E13.left")])]});
            var sketch = newSketch(context, id + "F7", { "sketchPlane" : qUnion([Q0])});
            skEllipse(sketch, "E14", {"center": v(-6.5, 16) * mm, "majorRadius": 4 * mm, "minorRadius": 4 * mm, "majorAxis": v(1, 0)});
            skEllipse(sketch, "E15.1.0.0", {"center": v(6.5, 16) * mm, "majorRadius": 4 * mm, "minorRadius": 4 * mm, "majorAxis": v(1, 0)});
            skLineSegment(sketch, "E15.direction1", {"start": v(-6.5, 16) * mm, "end": v(6.5, 16) * mm, "construction": true});
            skSolve(sketch);
        }
        {
            var Q0;
            Q0 = qSketchRegion(id + "F7", true);
            extrude(context, id + "F8", {"entities" : qUnion([Q0]), "operationType" : NewBodyOperationType.REMOVE, "endBound" : BoundingType.UP_TO_NEXT, "oppositeDirection" : true, "depth" : 25 * mm});
        }
        {
            var Q0;
            Q0=makeQuery(id+"F6.opExtrude","CAP_EDGE",EDGE,{"disambiguationData":[OSD([sQuery(id+"F5.wireOp",EDGE,"E13.bottom")])],"isStart":false});
            var Q1;
            Q1=makeQuery(id+"F6.opExtrude","CAP_EDGE",EDGE,{"disambiguationData":[OSD([sQuery(id+"F5.wireOp",EDGE,"E13.top")])],"isStart":false});
            fillet(context, id + "F9", {"entities" : qUnion([Q0, Q1]), "radius" : 5 * mm, "tangentPropagation" : true, "allowEdgeOverflow" : false});
        }
    });
